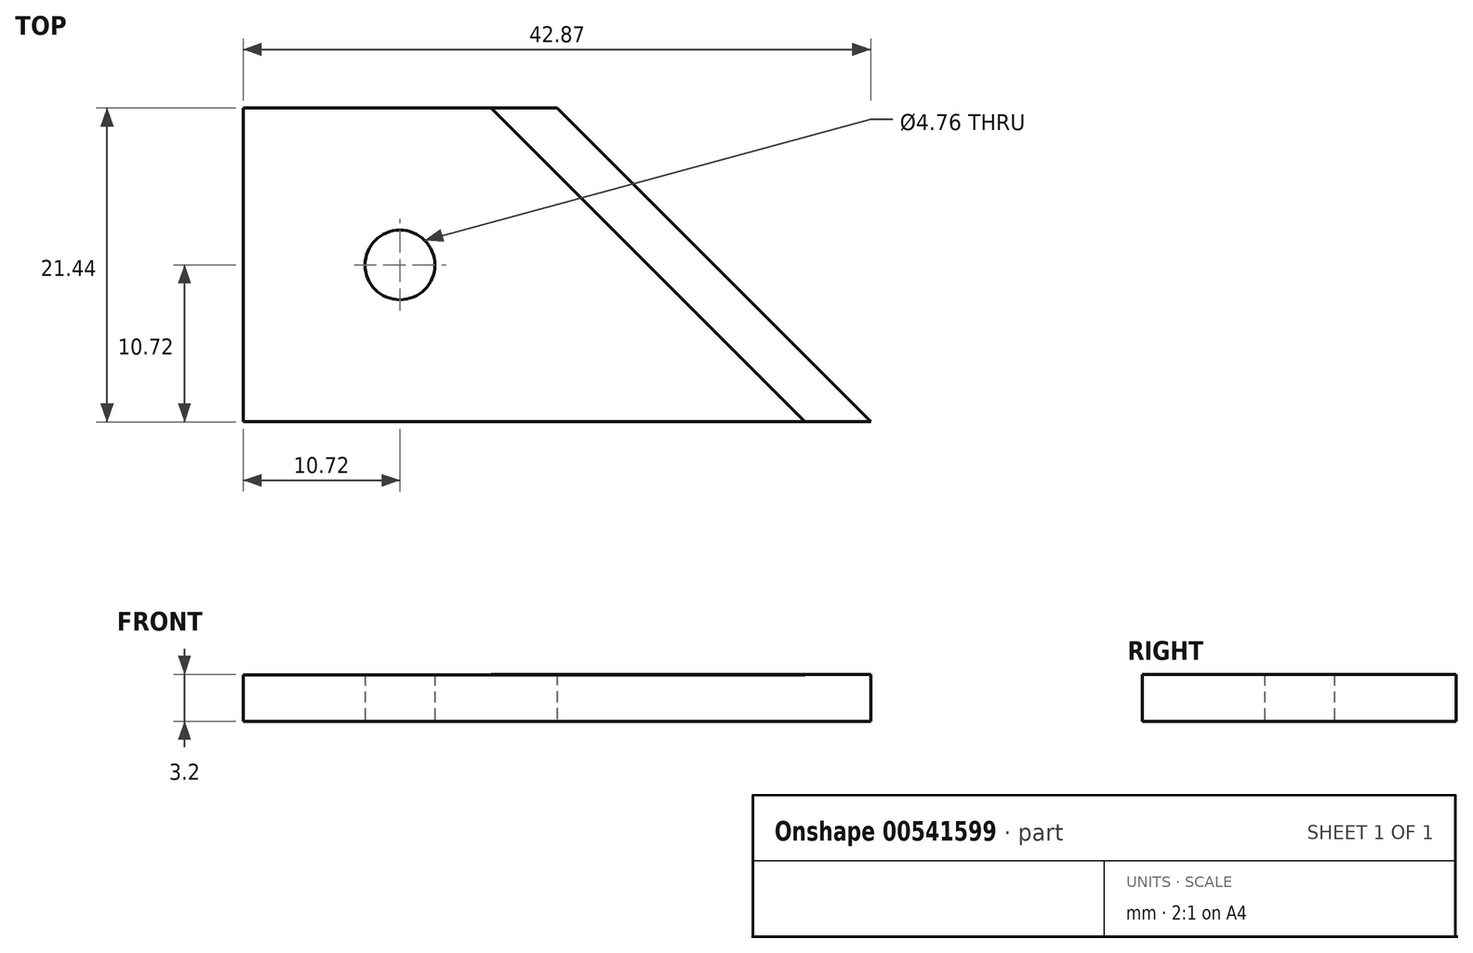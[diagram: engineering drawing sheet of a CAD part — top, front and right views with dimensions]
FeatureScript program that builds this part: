
annotation { "Feature Type Name" : "Feature", "Feature Type Description" : "" }
export const myFeature = defineFeature(function(context is Context, id is Id, definition is map)
    precondition{}
    {
        {
            var Q0;
            Q0=qCreatedBy(makeId("Top.planeOp"),FACE);
            var sketch = newSketch(context, id + "F0", { "sketchPlane" : qUnion([Q0])});
            skLineSegment(sketch, "E0.bottom", {"start": v(-10.72, 10.72) * mm, "end": v(10.72, 10.72) * mm});
            skLineSegment(sketch, "E0.top", {"start": v(-10.72, -10.72) * mm, "end": v(10.72, -10.72) * mm});
            skLineSegment(sketch, "E0.left", {"start": v(-10.72, 10.72) * mm, "end": v(-10.72, -10.72) * mm});
            skLineSegment(sketch, "E0.right", {"start": v(10.72, 10.72) * mm, "end": v(10.72, -10.72) * mm});
            skPoint(sketch, "E0.middle", {"position": v(0, 0) * mm});
            skLineSegment(sketch, "E1", {"start": v(10.72, -10.72) * mm, "end": v(32.15, -10.72) * mm});
            skLineSegment(sketch, "E2", {"start": v(32.15, -10.72) * mm, "end": v(10.72, 10.72) * mm});
            skCircle(sketch, "E3", {"center": v(0, 0) * mm, "radius": 2.38 * mm});
            skSolve(sketch);
        }
        {
            var Q0;
            Q0 = qSketchRegion(id + "F0", true);
            extrude(context, id + "F1", {"entities" : qUnion([Q0]), "depth" : 3.17 * mm, "offsetDistance" : 25.4 * mm});
        }
        {
            var Q0;
            Q0=makeQuery(id+"F1.opExtrude","CAP_FACE",FACE,{"disambiguationData":[OSD([sQuery(id+"F0.wireOp",EDGE,"E0.bottom"),sQuery(id+"F0.wireOp",EDGE,"E0.top"),sQuery(id+"F0.wireOp",EDGE,"E0.left"),sQuery(id+"F0.wireOp",EDGE,"E1"),sQuery(id+"F0.wireOp",EDGE,"E2")])],"isStart":false});
            var sketch = newSketch(context, id + "F2", { "sketchPlane" : qUnion([Q0])});
            skLineSegment(sketch, "E4", {"start": v(10.72, 10.72) * mm, "end": v(32.15, -10.72) * mm});
            skLineSegment(sketch, "E5", {"start": v(32.15, -10.72) * mm, "end": v(27.66, -10.72) * mm});
            skLineSegment(sketch, "E6", {"start": v(10.72, 10.72) * mm, "end": v(8.47, 8.47) * mm});
            skLineSegment(sketch, "E7", {"start": v(8.47, 8.47) * mm, "end": v(27.66, -10.72) * mm});
            skLineSegment(sketch, "E8", {"start": v(8.47, 8.47) * mm, "end": v(6.23, 10.72) * mm});
            skLineSegment(sketch, "E9", {"start": v(6.23, 10.72) * mm, "end": v(10.72, 10.72) * mm});
            skSolve(sketch);
        }
        {
            var Q0;
            Q0 = qSketchRegion(id + "F2", true);
            extrude(context, id + "F3", {"entities" : qUnion([Q0]), "operationType" : NewBodyOperationType.ADD, "depth" : 11.5 / 406.4 * mm, "offsetDistance" : 25.4 * mm});
        }
    });
